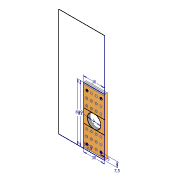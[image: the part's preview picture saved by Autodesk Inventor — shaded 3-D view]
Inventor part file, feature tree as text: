
AUTODESK INVENTOR PART (.ipt)
format: ipt  version: 2020.3 (Build 243373000, 373)  size: 200,704 bytes
history: native  units: mm
features: extrude x4, sketch x3, imported_body x1, pattern_linear x1, fillet x1
ambient origin geometry x8: Origin, YZ Plane, XZ Plane, XY Plane, X Axis, Y Axis, Z Axis, Center Point
bodies: Solid1 (feature_tree)
feature tree (10):
  imported_body  "Base1"
  sketch  "Sketch3"  dims[d21=30.0mm d22=81.0mm]
  extrude  "Extrusion3"  Depth=81.0mm
  extrude  "Extrusion4"  Depth=7.5mm
  pattern_linear  "Rectangular Pattern1"  Spacing1=5.0mm  [1 undecoded]
  sketch  "Sketch4"  dims[d23=5.0mm d24=7.5mm]
  sketch  "Sketch5"  dims[d25=5.0mm d26=0.0mm d27=5.0mm d28=7.5mm d29=10.0mm d30=0.0mm d31=80.0mm d33=9.4mm d34=40.0mm d36=6.7mm d37=30.0mm d38=81.0mm d39=10.0mm d40=0.0mm d41=19.0mm d42=10.0mm d43=0.0mm d44=2.0mm]
  extrude  "Extrusion5"  Depth=2.0mm
  extrude  "Extrusion6"  Depth=10.0mm TaperAngle=0.0deg
  fillet  "Fillet1"  Radius=80.0mm
note: 1 required parameter value undecoded (feature->parameter linkage not recoverable at this tier; creation-order binding heuristic only, values carry confidence <= 0.55)
